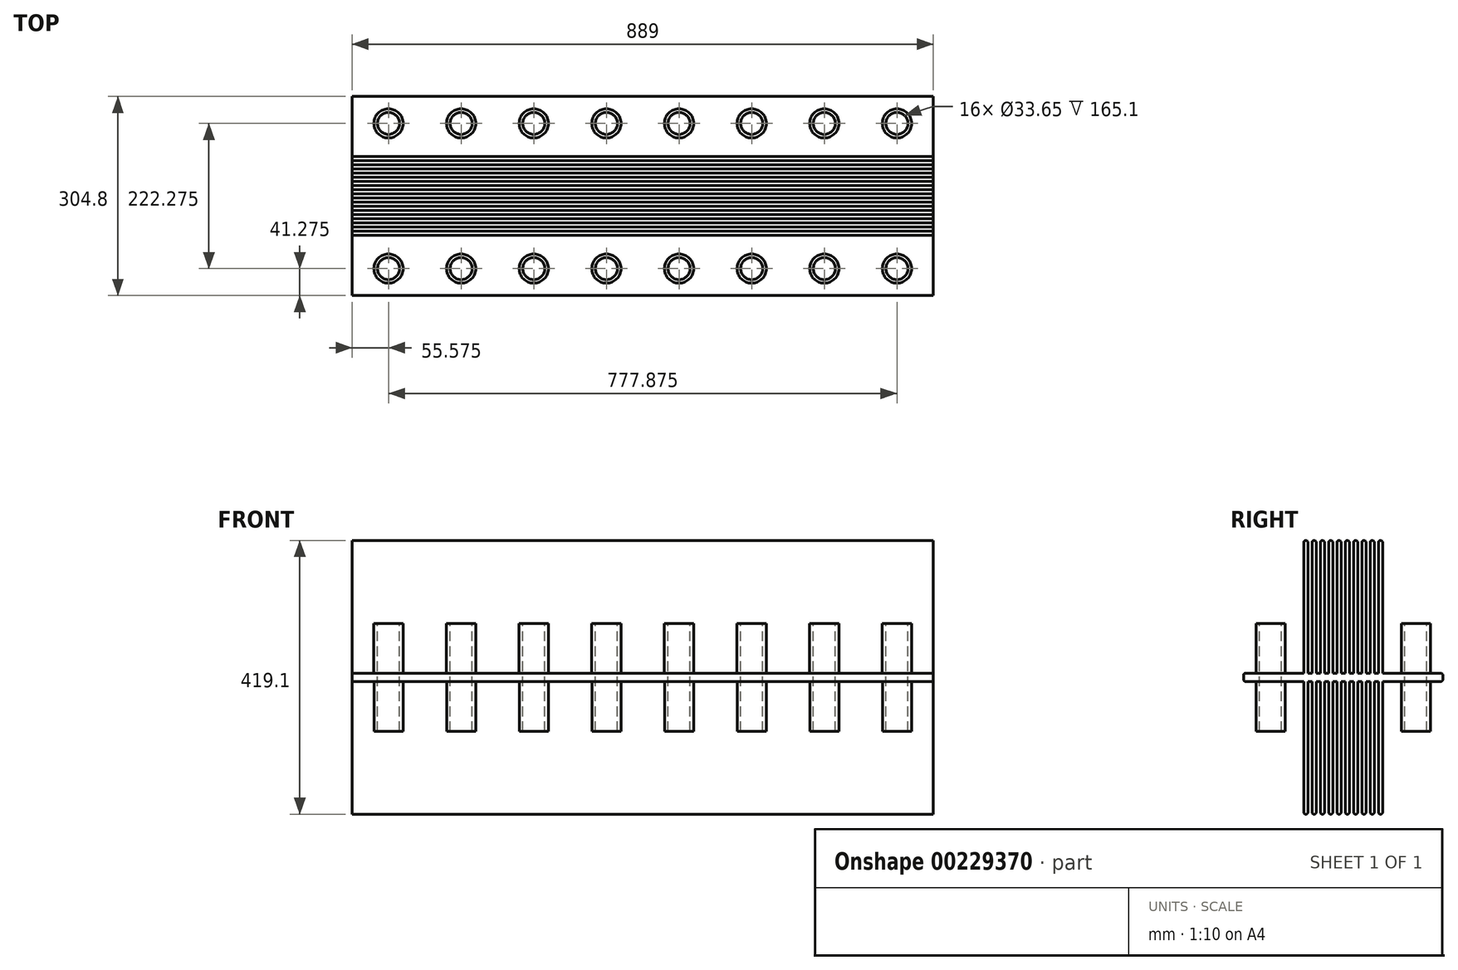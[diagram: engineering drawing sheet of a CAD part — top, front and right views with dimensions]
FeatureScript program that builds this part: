
annotation { "Feature Type Name" : "Feature", "Feature Type Description" : "" }
export const myFeature = defineFeature(function(context is Context, id is Id, definition is map)
    precondition{}
    {
        {
            var Q0;
            Q0=qCreatedBy(makeId("Top.planeOp"),FACE);
            var sketch = newSketch(context, id + "F0", { "sketchPlane" : qUnion([Q0])});
            skLineSegment(sketch, "E0.bottom", {"start": v(0, 0) * mm, "end": v(889, 0) * mm});
            skLineSegment(sketch, "E0.top", {"start": v(0, 304.8) * mm, "end": v(889, 304.8) * mm});
            skLineSegment(sketch, "E0.left", {"start": v(0, 0) * mm, "end": v(0, 304.8) * mm});
            skLineSegment(sketch, "E0.right", {"start": v(889, 0) * mm, "end": v(889, 304.8) * mm});
            skSolve(sketch);
        }
        {
            var Q0;
            Q0=makeQuery(id+"F0.imprint","IMPRINT",FACE,{"disambiguationData":[TD([[makeQuery(id+"F0.imprint","IMPRINT",EDGE,{"derivedFrom":sQuery(id+"F0.wireOp",EDGE,"E0.bottom")}),1.0]])]});
            extrude(context, id + "F1", {"entities" : qUnion([Q0]), "depth" : 12.7 * mm});
        }
        {
            var Q0;
            Q0=makeQuery(id+"F1.opExtrude","CAP_FACE",FACE,{"disambiguationData":[OSD([sQuery(id+"F0.wireOp",EDGE,"E0.bottom"),sQuery(id+"F0.wireOp",EDGE,"E0.top"),sQuery(id+"F0.wireOp",EDGE,"E0.left"),sQuery(id+"F0.wireOp",EDGE,"E0.right")])],"isStart":false});
            var sketch = newSketch(context, id + "F2", { "sketchPlane" : qUnion([Q0])});
            skPoint(sketch, "E1", {"position": v(55.58, 41.28) * mm});
            skPoint(sketch, "E2.0.1.0", {"position": v(55.58, 263.55) * mm});
            skPoint(sketch, "E2.1.0.0", {"position": v(166.7, 41.28) * mm});
            skPoint(sketch, "E2.1.1.0", {"position": v(166.7, 263.55) * mm});
            skPoint(sketch, "E2.2.0.0", {"position": v(277.83, 41.28) * mm});
            skPoint(sketch, "E2.2.1.0", {"position": v(277.83, 263.55) * mm});
            skPoint(sketch, "E2.3.0.0", {"position": v(388.95, 41.28) * mm});
            skPoint(sketch, "E2.3.1.0", {"position": v(388.95, 263.55) * mm});
            skPoint(sketch, "E2.4.0.0", {"position": v(500.08, 41.28) * mm});
            skPoint(sketch, "E2.4.1.0", {"position": v(500.08, 263.55) * mm});
            skPoint(sketch, "E2.5.0.0", {"position": v(611.2, 41.28) * mm});
            skPoint(sketch, "E2.5.1.0", {"position": v(611.2, 263.55) * mm});
            skPoint(sketch, "E2.6.0.0", {"position": v(722.33, 41.28) * mm});
            skPoint(sketch, "E2.6.1.0", {"position": v(722.33, 263.55) * mm});
            skPoint(sketch, "E2.7.0.0", {"position": v(833.45, 41.28) * mm});
            skPoint(sketch, "E2.7.1.0", {"position": v(833.45, 263.55) * mm});
            skLineSegment(sketch, "E2.direction1", {"start": v(55.58, 41.28) * mm, "end": v(166.7, 41.28) * mm, "construction": true});
            skLineSegment(sketch, "E2.direction2", {"start": v(55.58, 41.28) * mm, "end": v(55.58, 263.55) * mm, "construction": true});
            skSolve(sketch);
        }
        {
            var Q0;
            Q0=sQuery(id+"F2.wireOp",VERTEX,"E2.0.1.0");
            var Q1;
            Q1=sQuery(id+"F2.wireOp",VERTEX,"E2.1.1.0");
            var Q2;
            Q2=sQuery(id+"F2.wireOp",VERTEX,"E2.2.1.0");
            var Q3;
            Q3=sQuery(id+"F2.wireOp",VERTEX,"E2.3.1.0");
            var Q4;
            Q4=sQuery(id+"F2.wireOp",VERTEX,"E2.4.1.0");
            var Q5;
            Q5=sQuery(id+"F2.wireOp",VERTEX,"E2.5.1.0");
            var Q6;
            Q6=sQuery(id+"F2.wireOp",VERTEX,"E2.6.1.0");
            var Q7;
            Q7=sQuery(id+"F2.wireOp",VERTEX,"E2.7.1.0");
            var Q8;
            Q8=sQuery(id+"F2.wireOp",VERTEX,"E2.7.0.0");
            var Q9;
            Q9=sQuery(id+"F2.wireOp",VERTEX,"E2.6.0.0");
            var Q10;
            Q10=sQuery(id+"F2.wireOp",VERTEX,"E2.5.0.0");
            var Q11;
            Q11=sQuery(id+"F2.wireOp",VERTEX,"E2.4.0.0");
            var Q12;
            Q12=sQuery(id+"F2.wireOp",VERTEX,"E2.2.0.0");
            var Q13;
            Q13=sQuery(id+"F2.wireOp",VERTEX,"E2.1.0.0");
            var Q14;
            Q14=sQuery(id+"F2.wireOp",VERTEX,"E1");
            var Q15;
            Q15=sQuery(id+"F2.wireOp",VERTEX,"E2.3.0.0");
            var Q16;
            Q16=makeQuery(id+"F1.opExtrude","SWEPT_BODY",BODY,{"disambiguationData":[OSD([sQuery(id+"F0.wireOp",EDGE,"E0.bottom"),sQuery(id+"F0.wireOp",EDGE,"E0.top"),sQuery(id+"F0.wireOp",EDGE,"E0.left"),sQuery(id+"F0.wireOp",EDGE,"E0.right")])]});
            hole(context, id + "F3", {"style" : HoleStyle.SIMPLE, "endStyle" : HoleEndStyle.THROUGH, "holeDiameter" : 33.65 * mm, "locations" : qUnion([Q0, Q1, Q2, Q3, Q4, Q5, Q6, Q7, Q8, Q9, Q10, Q11, Q12, Q13, Q14, Q15]), "scope" : qUnion([Q16]), "isTappedThrough" : true});
        }
        {
            var Q0;
            Q0=makeQuery(id+"F1.opExtrude","SWEPT_FACE",FACE,{"disambiguationData":[OSD([sQuery(id+"F0.wireOp",EDGE,"E0.left")])]});
            var sketch = newSketch(context, id + "F4", { "sketchPlane" : qUnion([Q0])});
            skLineSegment(sketch, "E3", {"start": v(-304.8, 6.35) * mm, "end": v(0, 6.35) * mm, "construction": true});
            skPoint(sketch, "E4", {"position": v(-152.4, 6.35) * mm});
            skLineSegment(sketch, "E5", {"start": v(-152.4, 6.35) * mm, "end": v(-152.4, 94.18) * mm, "construction": true});
            skPoint(sketch, "E5.endSnap0", {"position": v(-152.4, 12.7) * mm});
            skLineSegment(sketch, "E6.bottom", {"start": v(-155.58, 12.7) * mm, "end": v(-161.93, 12.7) * mm});
            skLineSegment(sketch, "E6.top", {"start": v(-158.75, 215.9) * mm, "end": v(-158.75, 215.9) * mm});
            skLineSegment(sketch, "E6.left", {"start": v(-155.58, 12.7) * mm, "end": v(-155.58, 212.72) * mm});
            skLineSegment(sketch, "E6.right", {"start": v(-161.93, 12.7) * mm, "end": v(-161.93, 212.72) * mm});
            skLineSegment(sketch, "E7.bottom", {"start": v(-168.28, 12.7) * mm, "end": v(-174.62, 12.7) * mm});
            skLineSegment(sketch, "E7.top", {"start": v(-171.45, 215.9) * mm, "end": v(-171.45, 215.9) * mm});
            skLineSegment(sketch, "E7.left", {"start": v(-168.28, 12.7) * mm, "end": v(-168.28, 212.72) * mm});
            skLineSegment(sketch, "E7.right", {"start": v(-174.62, 12.7) * mm, "end": v(-174.63, 212.72) * mm});
            skLineSegment(sketch, "E8.bottom", {"start": v(-180.97, 12.7) * mm, "end": v(-187.32, 12.7) * mm});
            skLineSegment(sketch, "E8.top", {"start": v(-184.15, 215.9) * mm, "end": v(-184.15, 215.9) * mm});
            skLineSegment(sketch, "E8.left", {"start": v(-180.97, 12.7) * mm, "end": v(-180.98, 212.72) * mm});
            skLineSegment(sketch, "E8.right", {"start": v(-187.32, 12.7) * mm, "end": v(-187.33, 212.72) * mm});
            skLineSegment(sketch, "E9.bottom", {"start": v(-193.67, 12.7) * mm, "end": v(-200.02, 12.7) * mm});
            skLineSegment(sketch, "E9.top", {"start": v(-196.85, 215.9) * mm, "end": v(-196.85, 215.9) * mm});
            skLineSegment(sketch, "E9.left", {"start": v(-193.67, 12.7) * mm, "end": v(-193.68, 212.72) * mm});
            skLineSegment(sketch, "E9.right", {"start": v(-200.02, 12.7) * mm, "end": v(-200.03, 212.72) * mm});
            skLineSegment(sketch, "E10.bottom", {"start": v(-212.72, 12.7) * mm, "end": v(-206.37, 12.7) * mm});
            skLineSegment(sketch, "E10.top", {"start": v(-209.55, 215.9) * mm, "end": v(-209.55, 215.9) * mm});
            skLineSegment(sketch, "E10.left", {"start": v(-212.72, 12.7) * mm, "end": v(-212.72, 212.72) * mm});
            skLineSegment(sketch, "E10.right", {"start": v(-206.37, 12.7) * mm, "end": v(-206.38, 212.72) * mm});
            skLineSegment(sketch, "E11.MirrorCS", {"start": v(-149.23, 12.7) * mm, "end": v(-149.23, 212.72) * mm});
            skLineSegment(sketch, "E12.MirrorCS", {"start": v(-92.08, 12.7) * mm, "end": v(-92.08, 212.72) * mm});
            skLineSegment(sketch, "E13.MirrorCS", {"start": v(-98.43, 12.7) * mm, "end": v(-98.42, 212.72) * mm});
            skLineSegment(sketch, "E14.MirrorCS", {"start": v(-104.78, 12.7) * mm, "end": v(-104.77, 212.72) * mm});
            skLineSegment(sketch, "E15.MirrorCS", {"start": v(-111.13, 12.7) * mm, "end": v(-111.12, 212.72) * mm});
            skLineSegment(sketch, "E16.MirrorCS", {"start": v(-117.48, 12.7) * mm, "end": v(-117.47, 212.72) * mm});
            skLineSegment(sketch, "E17.MirrorCS", {"start": v(-123.83, 12.7) * mm, "end": v(-123.82, 212.72) * mm});
            skLineSegment(sketch, "E18.MirrorCS", {"start": v(-130.18, 12.7) * mm, "end": v(-130.17, 212.72) * mm});
            skLineSegment(sketch, "E19.MirrorCS", {"start": v(-136.53, 12.7) * mm, "end": v(-136.52, 212.72) * mm});
            skLineSegment(sketch, "E20.MirrorCS", {"start": v(-142.88, 12.7) * mm, "end": v(-142.87, 212.72) * mm});
            skLineSegment(sketch, "E21.MirrorCS", {"start": v(-149.22, 12.7) * mm, "end": v(-149.22, 212.72) * mm});
            skLineSegment(sketch, "E22.MirrorCS", {"start": v(-146.05, 215.9) * mm, "end": v(-146.05, 215.9) * mm});
            skLineSegment(sketch, "E23.MirrorCS", {"start": v(-133.35, 215.9) * mm, "end": v(-133.35, 215.9) * mm});
            skLineSegment(sketch, "E24.MirrorCS", {"start": v(-120.65, 215.9) * mm, "end": v(-120.65, 215.9) * mm});
            skLineSegment(sketch, "E25.MirrorCS", {"start": v(-107.95, 215.9) * mm, "end": v(-107.95, 215.9) * mm});
            skLineSegment(sketch, "E26.MirrorCS", {"start": v(-95.25, 215.9) * mm, "end": v(-95.25, 215.9) * mm});
            skLineSegment(sketch, "E27.MirrorCS", {"start": v(0, 6.35) * mm, "end": v(-304.8, 6.35) * mm, "construction": true});
            skLineSegment(sketch, "E28.MirrorCS", {"start": v(-149.22, 12.7) * mm, "end": v(-142.88, 12.7) * mm});
            skLineSegment(sketch, "E29.MirrorCS", {"start": v(-136.53, 12.7) * mm, "end": v(-130.18, 12.7) * mm});
            skLineSegment(sketch, "E30.MirrorCS", {"start": v(-123.83, 12.7) * mm, "end": v(-117.48, 12.7) * mm});
            skLineSegment(sketch, "E31.MirrorCS", {"start": v(-111.13, 12.7) * mm, "end": v(-104.78, 12.7) * mm});
            skLineSegment(sketch, "E32", {"start": v(-98.43, 12.7) * mm, "end": v(-92.08, 12.7) * mm});
            skPoint(sketch, "E33.visualSharp", {"position": v(-212.72, 215.9) * mm});
            skArc(sketch, "E33.filletArc", {"start": v(-209.55, 215.9) * mm, "mid": v(-211.8, 214.97) * mm, "end": v(-212.73, 212.72) * mm});
            skPoint(sketch, "E34.visualSharp", {"position": v(-206.38, 215.9) * mm});
            skArc(sketch, "E34.filletArc", {"start": v(-206.38, 212.72) * mm, "mid": v(-207.3, 214.97) * mm, "end": v(-209.55, 215.9) * mm});
            skPoint(sketch, "E35.visualSharp", {"position": v(-200.03, 215.9) * mm});
            skArc(sketch, "E35.filletArc", {"start": v(-196.85, 215.9) * mm, "mid": v(-199.1, 214.97) * mm, "end": v(-200.03, 212.72) * mm});
            skPoint(sketch, "E36.visualSharp", {"position": v(-193.68, 215.9) * mm});
            skArc(sketch, "E36.filletArc", {"start": v(-193.68, 212.72) * mm, "mid": v(-194.6, 214.97) * mm, "end": v(-196.85, 215.9) * mm});
            skPoint(sketch, "E37.visualSharp", {"position": v(-187.33, 215.9) * mm});
            skArc(sketch, "E37.filletArc", {"start": v(-184.15, 215.9) * mm, "mid": v(-186.4, 214.97) * mm, "end": v(-187.33, 212.72) * mm});
            skPoint(sketch, "E38.visualSharp", {"position": v(-180.98, 215.9) * mm});
            skArc(sketch, "E38.filletArc", {"start": v(-180.98, 212.72) * mm, "mid": v(-181.9, 214.97) * mm, "end": v(-184.15, 215.9) * mm});
            skPoint(sketch, "E39.visualSharp", {"position": v(-174.63, 215.9) * mm});
            skArc(sketch, "E39.filletArc", {"start": v(-171.45, 215.9) * mm, "mid": v(-173.7, 214.97) * mm, "end": v(-174.63, 212.72) * mm});
            skPoint(sketch, "E40.visualSharp", {"position": v(-168.28, 215.9) * mm});
            skArc(sketch, "E40.filletArc", {"start": v(-168.28, 212.72) * mm, "mid": v(-169.2, 214.97) * mm, "end": v(-171.45, 215.9) * mm});
            skPoint(sketch, "E41.visualSharp", {"position": v(-161.93, 215.9) * mm});
            skArc(sketch, "E41.filletArc", {"start": v(-158.75, 215.9) * mm, "mid": v(-161, 214.97) * mm, "end": v(-161.93, 212.72) * mm});
            skPoint(sketch, "E42.visualSharp", {"position": v(-155.58, 215.9) * mm});
            skArc(sketch, "E42.filletArc", {"start": v(-155.58, 212.72) * mm, "mid": v(-156.5, 214.97) * mm, "end": v(-158.75, 215.9) * mm});
            skPoint(sketch, "E43.visualSharp", {"position": v(-149.22, 215.9) * mm});
            skArc(sketch, "E43.filletArc", {"start": v(-146.05, 215.9) * mm, "mid": v(-148.3, 214.97) * mm, "end": v(-149.22, 212.72) * mm});
            skPoint(sketch, "E44.visualSharp", {"position": v(-142.87, 215.9) * mm});
            skArc(sketch, "E44.filletArc", {"start": v(-142.87, 212.72) * mm, "mid": v(-143.8, 214.97) * mm, "end": v(-146.05, 215.9) * mm});
            skPoint(sketch, "E45.visualSharp", {"position": v(-136.52, 215.9) * mm});
            skArc(sketch, "E45.filletArc", {"start": v(-133.35, 215.9) * mm, "mid": v(-135.6, 214.97) * mm, "end": v(-136.52, 212.72) * mm});
            skPoint(sketch, "E46.visualSharp", {"position": v(-130.17, 215.9) * mm});
            skArc(sketch, "E46.filletArc", {"start": v(-130.17, 212.72) * mm, "mid": v(-131.1, 214.97) * mm, "end": v(-133.35, 215.9) * mm});
            skPoint(sketch, "E47.visualSharp", {"position": v(-123.82, 215.9) * mm});
            skArc(sketch, "E47.filletArc", {"start": v(-120.65, 215.9) * mm, "mid": v(-122.9, 214.97) * mm, "end": v(-123.82, 212.72) * mm});
            skPoint(sketch, "E48.visualSharp", {"position": v(-117.47, 215.9) * mm});
            skArc(sketch, "E48.filletArc", {"start": v(-117.47, 212.72) * mm, "mid": v(-118.4, 214.97) * mm, "end": v(-120.65, 215.9) * mm});
            skPoint(sketch, "E49.visualSharp", {"position": v(-98.43, 215.9) * mm});
            skArc(sketch, "E49.filletArc", {"start": v(-95.25, 215.9) * mm, "mid": v(-97.5, 214.97) * mm, "end": v(-98.43, 212.72) * mm});
            skPoint(sketch, "E50.visualSharp", {"position": v(-92.08, 215.9) * mm});
            skArc(sketch, "E50.filletArc", {"start": v(-92.08, 212.72) * mm, "mid": v(-93, 214.97) * mm, "end": v(-95.25, 215.9) * mm});
            skPoint(sketch, "E51.visualSharp", {"position": v(-111.12, 215.9) * mm});
            skArc(sketch, "E51.filletArc", {"start": v(-107.95, 215.9) * mm, "mid": v(-110.2, 214.97) * mm, "end": v(-111.12, 212.72) * mm});
            skPoint(sketch, "E52.visualSharp", {"position": v(-104.78, 215.9) * mm});
            skArc(sketch, "E52.filletArc", {"start": v(-104.77, 212.72) * mm, "mid": v(-105.7, 214.97) * mm, "end": v(-107.95, 215.9) * mm});
            skLineSegment(sketch, "E53.MirrorCS", {"start": v(-212.72, 0) * mm, "end": v(-212.72, -200.02) * mm});
            skLineSegment(sketch, "E54.MirrorCS", {"start": v(-212.72, 0) * mm, "end": v(-206.37, 0) * mm});
            skLineSegment(sketch, "E55.MirrorCS", {"start": v(-206.37, 0) * mm, "end": v(-206.38, -200.02) * mm});
            skArc(sketch, "E56.MirrorCS", {"start": v(-209.55, -203.2) * mm, "mid": v(-211.8, -202.27) * mm, "end": v(-212.73, -200.02) * mm});
            skArc(sketch, "E57.MirrorCS", {"start": v(-206.38, -200.02) * mm, "mid": v(-207.3, -202.27) * mm, "end": v(-209.55, -203.2) * mm});
            skArc(sketch, "E58.MirrorCS", {"start": v(-196.85, -203.2) * mm, "mid": v(-199.1, -202.27) * mm, "end": v(-200.03, -200.02) * mm});
            skArc(sketch, "E59.MirrorCS", {"start": v(-193.68, -200.02) * mm, "mid": v(-194.6, -202.27) * mm, "end": v(-196.85, -203.2) * mm});
            skArc(sketch, "E60.MirrorCS", {"start": v(-184.15, -203.2) * mm, "mid": v(-186.4, -202.27) * mm, "end": v(-187.33, -200.02) * mm});
            skArc(sketch, "E61.MirrorCS", {"start": v(-180.98, -200.02) * mm, "mid": v(-181.9, -202.27) * mm, "end": v(-184.15, -203.2) * mm});
            skArc(sketch, "E62.MirrorCS", {"start": v(-171.45, -203.2) * mm, "mid": v(-173.7, -202.27) * mm, "end": v(-174.63, -200.02) * mm});
            skArc(sketch, "E63.MirrorCS", {"start": v(-168.28, -200.02) * mm, "mid": v(-169.2, -202.27) * mm, "end": v(-171.45, -203.2) * mm});
            skArc(sketch, "E64.MirrorCS", {"start": v(-158.75, -203.2) * mm, "mid": v(-161, -202.27) * mm, "end": v(-161.93, -200.02) * mm});
            skArc(sketch, "E65.MirrorCS", {"start": v(-155.58, -200.02) * mm, "mid": v(-156.5, -202.27) * mm, "end": v(-158.75, -203.2) * mm});
            skArc(sketch, "E66.MirrorCS", {"start": v(-92.08, -200.02) * mm, "mid": v(-93, -202.27) * mm, "end": v(-95.25, -203.2) * mm});
            skArc(sketch, "E67.MirrorCS", {"start": v(-95.25, -203.2) * mm, "mid": v(-97.5, -202.27) * mm, "end": v(-98.43, -200.02) * mm});
            skArc(sketch, "E68.MirrorCS", {"start": v(-104.77, -200.02) * mm, "mid": v(-105.7, -202.27) * mm, "end": v(-107.95, -203.2) * mm});
            skArc(sketch, "E69.MirrorCS", {"start": v(-107.95, -203.2) * mm, "mid": v(-110.2, -202.27) * mm, "end": v(-111.12, -200.02) * mm});
            skArc(sketch, "E70.MirrorCS", {"start": v(-117.47, -200.02) * mm, "mid": v(-118.4, -202.27) * mm, "end": v(-120.65, -203.2) * mm});
            skArc(sketch, "E71.MirrorCS", {"start": v(-120.65, -203.2) * mm, "mid": v(-122.9, -202.27) * mm, "end": v(-123.82, -200.02) * mm});
            skArc(sketch, "E72.MirrorCS", {"start": v(-130.17, -200.02) * mm, "mid": v(-131.1, -202.27) * mm, "end": v(-133.35, -203.2) * mm});
            skArc(sketch, "E73.MirrorCS", {"start": v(-133.35, -203.2) * mm, "mid": v(-135.6, -202.27) * mm, "end": v(-136.52, -200.02) * mm});
            skArc(sketch, "E74.MirrorCS", {"start": v(-142.87, -200.02) * mm, "mid": v(-143.8, -202.27) * mm, "end": v(-146.05, -203.2) * mm});
            skArc(sketch, "E75.MirrorCS", {"start": v(-146.05, -203.2) * mm, "mid": v(-148.3, -202.27) * mm, "end": v(-149.22, -200.02) * mm});
            skLineSegment(sketch, "E76.MirrorCS", {"start": v(-187.32, 0) * mm, "end": v(-187.33, -200.02) * mm});
            skLineSegment(sketch, "E77.MirrorCS", {"start": v(-180.97, 0) * mm, "end": v(-180.98, -200.02) * mm});
            skLineSegment(sketch, "E78.MirrorCS", {"start": v(-174.62, 0) * mm, "end": v(-174.63, -200.02) * mm});
            skLineSegment(sketch, "E79.MirrorCS", {"start": v(-168.28, 0) * mm, "end": v(-168.28, -200.02) * mm});
            skLineSegment(sketch, "E80.MirrorCS", {"start": v(-161.93, 0) * mm, "end": v(-161.93, -200.02) * mm});
            skLineSegment(sketch, "E81.MirrorCS", {"start": v(-155.58, 0) * mm, "end": v(-155.58, -200.02) * mm});
            skLineSegment(sketch, "E82.MirrorCS", {"start": v(-149.23, 0) * mm, "end": v(-149.23, -200.02) * mm});
            skLineSegment(sketch, "E83.MirrorCS", {"start": v(-142.88, 0) * mm, "end": v(-142.87, -200.02) * mm});
            skLineSegment(sketch, "E84.MirrorCS", {"start": v(-136.53, 0) * mm, "end": v(-136.52, -200.02) * mm});
            skLineSegment(sketch, "E85.MirrorCS", {"start": v(-130.18, 0) * mm, "end": v(-130.17, -200.02) * mm});
            skLineSegment(sketch, "E86.MirrorCS", {"start": v(-123.83, 0) * mm, "end": v(-123.82, -200.02) * mm});
            skLineSegment(sketch, "E87.MirrorCS", {"start": v(-117.48, 0) * mm, "end": v(-117.47, -200.02) * mm});
            skLineSegment(sketch, "E88.MirrorCS", {"start": v(-111.13, 0) * mm, "end": v(-111.12, -200.02) * mm});
            skLineSegment(sketch, "E89.MirrorCS", {"start": v(-104.78, 0) * mm, "end": v(-104.77, -200.02) * mm});
            skLineSegment(sketch, "E90.MirrorCS", {"start": v(-98.43, 0) * mm, "end": v(-98.42, -200.02) * mm});
            skLineSegment(sketch, "E91.MirrorCS", {"start": v(-92.08, 0) * mm, "end": v(-92.08, -200.02) * mm});
            skLineSegment(sketch, "E92.MirrorCS", {"start": v(-193.67, 0) * mm, "end": v(-193.68, -200.02) * mm});
            skLineSegment(sketch, "E93.MirrorCS", {"start": v(-200.02, 0) * mm, "end": v(-200.03, -200.02) * mm});
            skLineSegment(sketch, "E94.MirrorCS", {"start": v(-193.67, 0) * mm, "end": v(-200.02, 0) * mm});
            skLineSegment(sketch, "E95.MirrorCS", {"start": v(-180.97, 0) * mm, "end": v(-187.32, 0) * mm});
            skLineSegment(sketch, "E96.MirrorCS", {"start": v(-168.28, 0) * mm, "end": v(-174.62, 0) * mm});
            skLineSegment(sketch, "E97.MirrorCS", {"start": v(-155.58, 0) * mm, "end": v(-161.93, 0) * mm});
            skLineSegment(sketch, "E98.MirrorCS", {"start": v(-149.22, 0) * mm, "end": v(-142.88, 0) * mm});
            skLineSegment(sketch, "E99.MirrorCS", {"start": v(-136.53, 0) * mm, "end": v(-130.18, 0) * mm});
            skLineSegment(sketch, "E100.MirrorCS", {"start": v(-123.83, 0) * mm, "end": v(-117.48, 0) * mm});
            skLineSegment(sketch, "E101.MirrorCS", {"start": v(-111.13, 0) * mm, "end": v(-104.78, 0) * mm});
            skLineSegment(sketch, "E102.MirrorCS", {"start": v(-98.43, 0) * mm, "end": v(-92.08, 0) * mm});
            skPoint(sketch, "E103.orphan", {"position": v(-149.23, -203.2) * mm});
            skPoint(sketch, "E104.orphan", {"position": v(-149.23, 215.9) * mm});
            skSolve(sketch);
        }
        {
            var Q0;
            Q0 = qSketchRegion(id + "F4", true);
            var Q1;
            Q1=makeQuery(id+"F1.opExtrude","SWEPT_FACE",FACE,{"disambiguationData":[OSD([sQuery(id+"F0.wireOp",EDGE,"E0.right")])]});
            extrude(context, id + "F5", {"entities" : qUnion([Q0]), "operationType" : NewBodyOperationType.ADD, "endBound" : BoundingType.UP_TO_SURFACE, "oppositeDirection" : true, "endBoundEntityFace" : qUnion([Q1]), "depth" : 25.4 * mm});
        }
        {
            var Q0;
            Q0=makeQuery(id+"F1.opExtrude","CAP_EDGE",EDGE,{"disambiguationData":[OSD([sQuery(id+"F0.wireOp",EDGE,"E0.bottom")])],"isStart":false});
            var Q1;
            Q1=makeQuery(id+"F1.opExtrude","CAP_EDGE",EDGE,{"disambiguationData":[OSD([sQuery(id+"F0.wireOp",EDGE,"E0.bottom")])],"isStart":true});
            var Q2;
            Q2=makeQuery(id+"F1.opExtrude","CAP_EDGE",EDGE,{"disambiguationData":[OSD([sQuery(id+"F0.wireOp",EDGE,"E0.top")])],"isStart":false});
            var Q3;
            Q3=makeQuery(id+"F1.opExtrude","CAP_EDGE",EDGE,{"disambiguationData":[OSD([sQuery(id+"F0.wireOp",EDGE,"E0.top")])],"isStart":true});
            fillet(context, id + "F6", {"entities" : qUnion([Q0, Q1, Q2, Q3]), "radius" : 3.17 * mm, "tangentPropagation" : true, "allowEdgeOverflow" : false});
        }
        {
            var Q0;
            {var subQ5=sQuery(id+"F0.wireOp",EDGE,"E0.right");var subQ81=sQuery(id+"F0.wireOp",EDGE,"E0.left");var subQ82=sQuery(id+"F0.wireOp",EDGE,"E0.bottom");Q0=makeQuery(id+"F5.boolean.opBoolean","SPLIT",FACE,{"disambiguationData":[TD([makeQuery(id+"F1.opExtrude","SWEPT_FACE",FACE,{"disambiguationData":[OSD([subQ82])]})])],"derivedFrom":makeQuery(id+"F1.opExtrude","CAP_FACE",FACE,{"disambiguationData":[OSD([subQ82,sQuery(id+"F0.wireOp",EDGE,"E0.top"),subQ81,subQ5])],"isStart":false})});}
            var sketch = newSketch(context, id + "F7", { "sketchPlane" : qUnion([Q0])});
            skCircle(sketch, "E105.0", {"center": v(55.58, 41.28) * mm, "radius": 16.83 * mm});
            skCircle(sketch, "E106", {"center": v(55.58, 41.28) * mm, "radius": 22.36 * mm});
            skCircle(sketch, "E107.0.1.0", {"center": v(55.58, 263.55) * mm, "radius": 22.36 * mm});
            skCircle(sketch, "E107.1.0.0", {"center": v(166.7, 41.28) * mm, "radius": 22.36 * mm});
            skCircle(sketch, "E107.1.1.0", {"center": v(166.7, 263.55) * mm, "radius": 22.36 * mm});
            skCircle(sketch, "E107.2.0.0", {"center": v(277.83, 41.28) * mm, "radius": 22.36 * mm});
            skCircle(sketch, "E107.2.1.0", {"center": v(277.83, 263.55) * mm, "radius": 22.36 * mm});
            skCircle(sketch, "E107.3.0.0", {"center": v(388.95, 41.28) * mm, "radius": 22.36 * mm});
            skCircle(sketch, "E107.3.1.0", {"center": v(388.95, 263.55) * mm, "radius": 22.36 * mm});
            skCircle(sketch, "E107.4.0.0", {"center": v(500.08, 41.28) * mm, "radius": 22.36 * mm});
            skCircle(sketch, "E107.4.1.0", {"center": v(500.08, 263.55) * mm, "radius": 22.36 * mm});
            skCircle(sketch, "E107.5.0.0", {"center": v(611.2, 41.28) * mm, "radius": 22.36 * mm});
            skCircle(sketch, "E107.5.1.0", {"center": v(611.2, 263.55) * mm, "radius": 22.36 * mm});
            skCircle(sketch, "E107.6.0.0", {"center": v(722.33, 41.28) * mm, "radius": 22.36 * mm});
            skCircle(sketch, "E107.6.1.0", {"center": v(722.33, 263.55) * mm, "radius": 22.36 * mm});
            skCircle(sketch, "E107.7.0.0", {"center": v(833.45, 41.28) * mm, "radius": 22.36 * mm});
            skCircle(sketch, "E107.7.1.0", {"center": v(833.45, 263.55) * mm, "radius": 22.36 * mm});
            skLineSegment(sketch, "E107.direction1", {"start": v(55.58, 41.28) * mm, "end": v(166.7, 41.28) * mm, "construction": true});
            skLineSegment(sketch, "E107.direction2", {"start": v(55.58, 41.28) * mm, "end": v(55.58, 263.55) * mm, "construction": true});
            skCircle(sketch, "E108.0", {"center": v(55.58, 263.55) * mm, "radius": 16.83 * mm});
            skCircle(sketch, "E109.0", {"center": v(166.7, 263.55) * mm, "radius": 16.83 * mm});
            skCircle(sketch, "E110.0", {"center": v(277.83, 263.55) * mm, "radius": 16.83 * mm});
            skCircle(sketch, "E111.0", {"center": v(388.95, 263.55) * mm, "radius": 16.83 * mm});
            skCircle(sketch, "E112.0", {"center": v(500.08, 263.55) * mm, "radius": 16.83 * mm});
            skCircle(sketch, "E113.0", {"center": v(611.2, 263.55) * mm, "radius": 16.83 * mm});
            skCircle(sketch, "E114.0", {"center": v(722.33, 263.55) * mm, "radius": 16.83 * mm});
            skCircle(sketch, "E115.0", {"center": v(833.45, 263.55) * mm, "radius": 16.83 * mm});
            skCircle(sketch, "E116.0", {"center": v(833.45, 41.28) * mm, "radius": 16.83 * mm});
            skCircle(sketch, "E117.0", {"center": v(722.33, 41.28) * mm, "radius": 16.83 * mm});
            skCircle(sketch, "E118.0", {"center": v(611.2, 41.28) * mm, "radius": 16.83 * mm});
            skCircle(sketch, "E119.0", {"center": v(500.08, 41.28) * mm, "radius": 16.83 * mm});
            skCircle(sketch, "E120.0", {"center": v(388.95, 41.28) * mm, "radius": 16.83 * mm});
            skCircle(sketch, "E121.0", {"center": v(277.83, 41.28) * mm, "radius": 16.83 * mm});
            skCircle(sketch, "E122.0", {"center": v(166.7, 41.28) * mm, "radius": 16.83 * mm});
            skSolve(sketch);
        }
        {
            var Q0;
            Q0 = qSketchRegion(id + "F7", true);
            extrude(context, id + "F8", {"entities" : qUnion([Q0]), "operationType" : NewBodyOperationType.ADD, "depth" : 76.2 * mm});
        }
        {
            var Q0;
            {var subQ5=sQuery(id+"F0.wireOp",EDGE,"E0.right");var subQ81=sQuery(id+"F0.wireOp",EDGE,"E0.left");var subQ87=sQuery(id+"F0.wireOp",EDGE,"E0.bottom");Q0=makeQuery(id+"F5.boolean.opBoolean","SPLIT",FACE,{"disambiguationData":[TD([makeQuery(id+"F1.opExtrude","SWEPT_FACE",FACE,{"disambiguationData":[OSD([subQ87])]})])],"derivedFrom":makeQuery(id+"F1.opExtrude","CAP_FACE",FACE,{"disambiguationData":[OSD([subQ87,sQuery(id+"F0.wireOp",EDGE,"E0.top"),subQ81,subQ5])],"isStart":true})});}
            var sketch = newSketch(context, id + "F9", { "sketchPlane" : qUnion([Q0])});
            skCircle(sketch, "E123.0", {"center": v(55.58, -263.55) * mm, "radius": 16.83 * mm});
            skCircle(sketch, "E124.0", {"center": v(166.7, -263.55) * mm, "radius": 16.83 * mm});
            skCircle(sketch, "E125.0", {"center": v(166.7, -41.28) * mm, "radius": 16.83 * mm});
            skCircle(sketch, "E126.0", {"center": v(55.58, -41.28) * mm, "radius": 16.83 * mm});
            skCircle(sketch, "E127.0", {"center": v(277.83, -41.28) * mm, "radius": 16.83 * mm});
            skCircle(sketch, "E128.0", {"center": v(388.95, -41.28) * mm, "radius": 16.83 * mm});
            skCircle(sketch, "E129.0", {"center": v(500.08, -41.28) * mm, "radius": 16.83 * mm});
            skCircle(sketch, "E130.0", {"center": v(611.2, -41.28) * mm, "radius": 16.83 * mm});
            skCircle(sketch, "E131.0", {"center": v(833.45, -41.28) * mm, "radius": 16.83 * mm});
            skCircle(sketch, "E132.0", {"center": v(722.33, -41.28) * mm, "radius": 16.83 * mm});
            skCircle(sketch, "E133.0", {"center": v(722.33, -263.55) * mm, "radius": 16.83 * mm});
            skCircle(sketch, "E134.0", {"center": v(833.45, -263.55) * mm, "radius": 16.83 * mm});
            skCircle(sketch, "E135.0", {"center": v(611.2, -263.55) * mm, "radius": 16.83 * mm});
            skCircle(sketch, "E136.0", {"center": v(388.95, -263.55) * mm, "radius": 16.83 * mm});
            skCircle(sketch, "E137.0", {"center": v(500.08, -263.55) * mm, "radius": 16.83 * mm});
            skCircle(sketch, "E138.0", {"center": v(277.83, -263.55) * mm, "radius": 16.83 * mm});
            skCircle(sketch, "E139", {"center": v(55.58, -263.55) * mm, "radius": 22.24 * mm});
            skCircle(sketch, "E140.0.1.0", {"center": v(55.58, -41.28) * mm, "radius": 22.24 * mm});
            skCircle(sketch, "E140.1.0.0", {"center": v(166.7, -263.55) * mm, "radius": 22.24 * mm});
            skCircle(sketch, "E140.1.1.0", {"center": v(166.7, -41.28) * mm, "radius": 22.24 * mm});
            skCircle(sketch, "E140.2.0.0", {"center": v(277.83, -263.55) * mm, "radius": 22.24 * mm});
            skCircle(sketch, "E140.2.1.0", {"center": v(277.83, -41.28) * mm, "radius": 22.24 * mm});
            skCircle(sketch, "E140.3.0.0", {"center": v(388.95, -263.55) * mm, "radius": 22.24 * mm});
            skCircle(sketch, "E140.3.1.0", {"center": v(388.95, -41.28) * mm, "radius": 22.24 * mm});
            skCircle(sketch, "E140.4.0.0", {"center": v(500.08, -263.55) * mm, "radius": 22.24 * mm});
            skCircle(sketch, "E140.4.1.0", {"center": v(500.08, -41.28) * mm, "radius": 22.24 * mm});
            skCircle(sketch, "E140.5.0.0", {"center": v(611.2, -263.55) * mm, "radius": 22.24 * mm});
            skCircle(sketch, "E140.5.1.0", {"center": v(611.2, -41.28) * mm, "radius": 22.24 * mm});
            skCircle(sketch, "E140.6.0.0", {"center": v(722.33, -263.55) * mm, "radius": 22.24 * mm});
            skCircle(sketch, "E140.6.1.0", {"center": v(722.33, -41.28) * mm, "radius": 22.24 * mm});
            skCircle(sketch, "E140.7.0.0", {"center": v(833.45, -263.55) * mm, "radius": 22.24 * mm});
            skCircle(sketch, "E140.7.1.0", {"center": v(833.45, -41.28) * mm, "radius": 22.24 * mm});
            skLineSegment(sketch, "E140.direction1", {"start": v(55.58, -263.55) * mm, "end": v(166.7, -263.55) * mm, "construction": true});
            skLineSegment(sketch, "E140.direction2", {"start": v(55.58, -263.55) * mm, "end": v(55.58, -41.28) * mm, "construction": true});
            skSolve(sketch);
        }
        {
            var Q0;
            Q0=makeQuery(id+"F9.imprint","IMPRINT",FACE,{"disambiguationData":[TD([[makeQuery(id+"F9.imprint","IMPRINT",EDGE,{"derivedFrom":sQuery(id+"F9.wireOp",EDGE,"E123.0")}),-1.0]])]});
            var Q1;
            Q1=makeQuery(id+"F9.imprint","IMPRINT",FACE,{"disambiguationData":[TD([[makeQuery(id+"F9.imprint","IMPRINT",EDGE,{"derivedFrom":sQuery(id+"F9.wireOp",EDGE,"E138.0")}),-1.0]])]});
            var Q2;
            Q2=makeQuery(id+"F9.imprint","IMPRINT",FACE,{"disambiguationData":[TD([[makeQuery(id+"F9.imprint","IMPRINT",EDGE,{"derivedFrom":sQuery(id+"F9.wireOp",EDGE,"E129.0")}),-1.0]])]});
            var Q3;
            Q3=makeQuery(id+"F9.imprint","IMPRINT",FACE,{"disambiguationData":[TD([[makeQuery(id+"F9.imprint","IMPRINT",EDGE,{"derivedFrom":sQuery(id+"F9.wireOp",EDGE,"E128.0")}),-1.0]])]});
            var Q4;
            Q4=makeQuery(id+"F9.imprint","IMPRINT",FACE,{"disambiguationData":[TD([[makeQuery(id+"F9.imprint","IMPRINT",EDGE,{"derivedFrom":sQuery(id+"F9.wireOp",EDGE,"E127.0")}),-1.0]])]});
            var Q5;
            Q5=makeQuery(id+"F9.imprint","IMPRINT",FACE,{"disambiguationData":[TD([[makeQuery(id+"F9.imprint","IMPRINT",EDGE,{"derivedFrom":sQuery(id+"F9.wireOp",EDGE,"E125.0")}),-1.0]])]});
            var Q6;
            Q6=makeQuery(id+"F9.imprint","IMPRINT",FACE,{"disambiguationData":[TD([[makeQuery(id+"F9.imprint","IMPRINT",EDGE,{"derivedFrom":sQuery(id+"F9.wireOp",EDGE,"E126.0")}),-1.0]])]});
            var Q7;
            Q7=makeQuery(id+"F9.imprint","IMPRINT",FACE,{"disambiguationData":[TD([[makeQuery(id+"F9.imprint","IMPRINT",EDGE,{"derivedFrom":sQuery(id+"F9.wireOp",EDGE,"E130.0")}),-1.0]])]});
            var Q8;
            Q8=makeQuery(id+"F9.imprint","IMPRINT",FACE,{"disambiguationData":[TD([[makeQuery(id+"F9.imprint","IMPRINT",EDGE,{"derivedFrom":sQuery(id+"F9.wireOp",EDGE,"E132.0")}),-1.0]])]});
            var Q9;
            Q9=makeQuery(id+"F9.imprint","IMPRINT",FACE,{"disambiguationData":[TD([[makeQuery(id+"F9.imprint","IMPRINT",EDGE,{"derivedFrom":sQuery(id+"F9.wireOp",EDGE,"E131.0")}),-1.0]])]});
            var Q10;
            Q10=makeQuery(id+"F9.imprint","IMPRINT",FACE,{"disambiguationData":[TD([[makeQuery(id+"F9.imprint","IMPRINT",EDGE,{"derivedFrom":sQuery(id+"F9.wireOp",EDGE,"E134.0")}),-1.0]])]});
            var Q11;
            Q11=makeQuery(id+"F9.imprint","IMPRINT",FACE,{"disambiguationData":[TD([[makeQuery(id+"F9.imprint","IMPRINT",EDGE,{"derivedFrom":sQuery(id+"F9.wireOp",EDGE,"E133.0")}),-1.0]])]});
            var Q12;
            Q12=makeQuery(id+"F9.imprint","IMPRINT",FACE,{"disambiguationData":[TD([[makeQuery(id+"F9.imprint","IMPRINT",EDGE,{"derivedFrom":sQuery(id+"F9.wireOp",EDGE,"E135.0")}),-1.0]])]});
            var Q13;
            Q13=makeQuery(id+"F9.imprint","IMPRINT",FACE,{"disambiguationData":[TD([[makeQuery(id+"F9.imprint","IMPRINT",EDGE,{"derivedFrom":sQuery(id+"F9.wireOp",EDGE,"E137.0")}),-1.0]])]});
            var Q14;
            Q14=makeQuery(id+"F9.imprint","IMPRINT",FACE,{"disambiguationData":[TD([[makeQuery(id+"F9.imprint","IMPRINT",EDGE,{"derivedFrom":sQuery(id+"F9.wireOp",EDGE,"E136.0")}),-1.0]])]});
            var Q15;
            Q15=makeQuery(id+"F9.imprint","IMPRINT",FACE,{"disambiguationData":[TD([[makeQuery(id+"F9.imprint","IMPRINT",EDGE,{"derivedFrom":sQuery(id+"F9.wireOp",EDGE,"E124.0")}),-1.0]])]});
            extrude(context, id + "F10", {"entities" : qUnion([Q0, Q1, Q2, Q3, Q4, Q5, Q6, Q7, Q8, Q9, Q10, Q11, Q12, Q13, Q14, Q15]), "operationType" : NewBodyOperationType.ADD, "depth" : 76.2 * mm});
        }
    });
